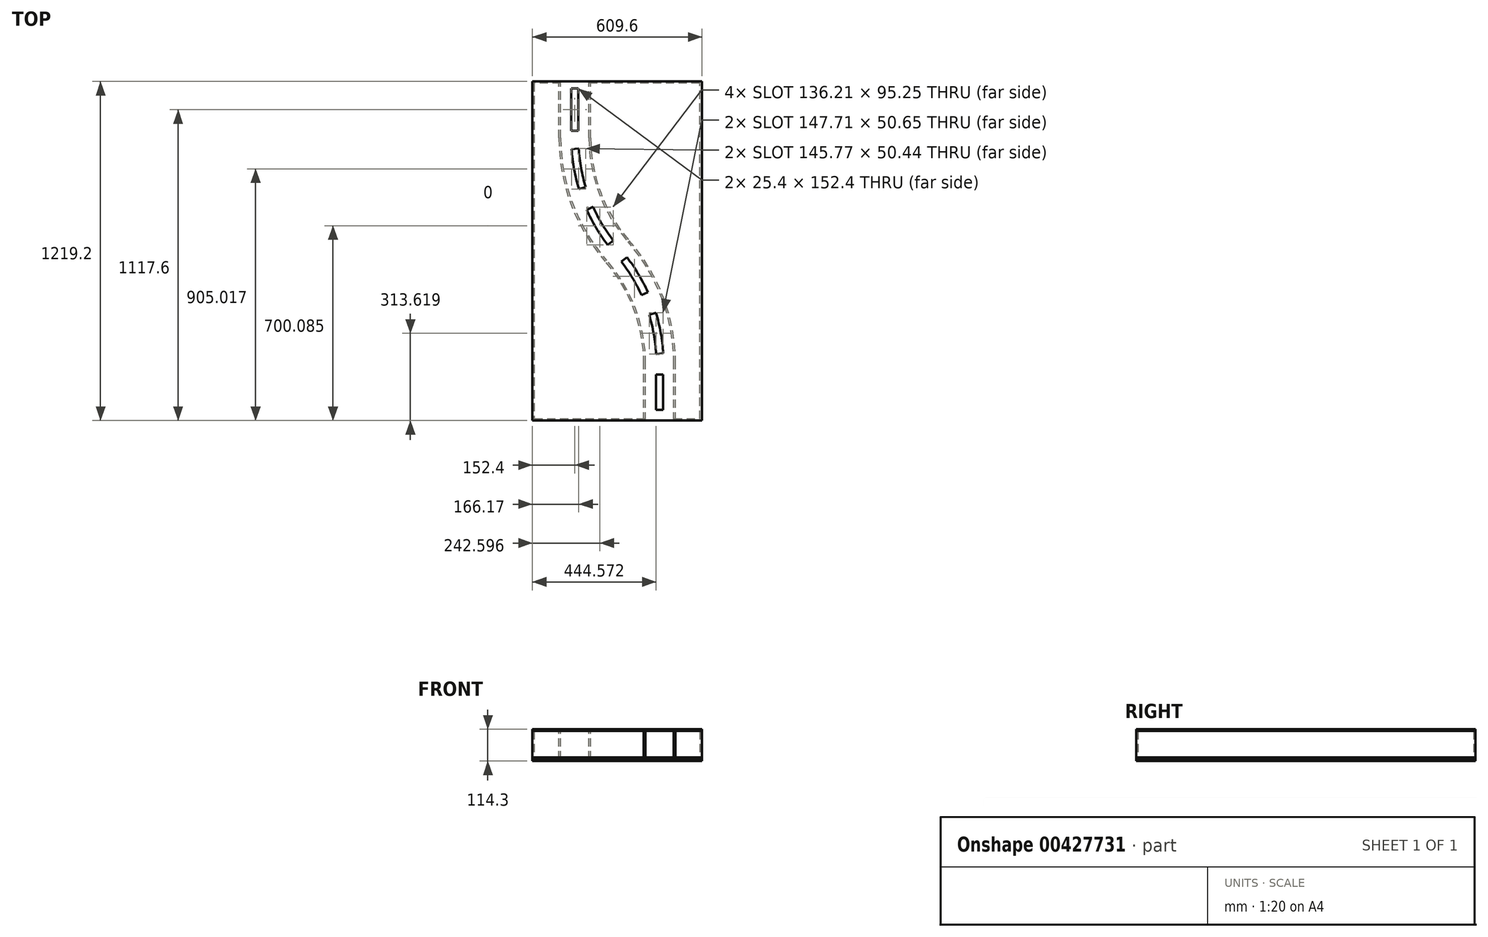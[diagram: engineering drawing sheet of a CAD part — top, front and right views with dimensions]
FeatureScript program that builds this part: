
annotation { "Feature Type Name" : "Feature", "Feature Type Description" : "" }
export const myFeature = defineFeature(function(context is Context, id is Id, definition is map)
    precondition{}
    {
        {
            var Q0;
            Q0=qCreatedBy(makeId("Top.planeOp"),FACE);
            var sketch = newSketch(context, id + "F0", { "sketchPlane" : qUnion([Q0])});
            skLineSegment(sketch, "E0.bottom", {"start": v(0, 0) * mm, "end": v(609.6, 0) * mm});
            skLineSegment(sketch, "E0.top", {"start": v(0, 1219.2) * mm, "end": v(609.6, 1219.2) * mm});
            skLineSegment(sketch, "E0.left", {"start": v(0, 0) * mm, "end": v(0, 1219.2) * mm});
            skLineSegment(sketch, "E0.right", {"start": v(609.6, 0) * mm, "end": v(609.6, 1219.2) * mm});
            skLineSegment(sketch, "E1", {"start": v(406.4, 0) * mm, "end": v(406.4, 203.2) * mm});
            skLineSegment(sketch, "E2", {"start": v(508, 0) * mm, "end": v(508, 203.2) * mm});
            skArc(sketch, "E3", {"start": v(406.4, 203.2) * mm, "mid": v(370.28, 402.38) * mm, "end": v(266.53, 576.2) * mm});
            skArc(sketch, "E4", {"start": v(508, 203.2) * mm, "mid": v(465.41, 438.05) * mm, "end": v(343.07, 643) * mm});
            skLineSegment(sketch, "E5", {"start": v(-160.87, 203.2) * mm, "end": v(343.07, 643) * mm, "construction": true});
            skArc(sketch, "E6", {"start": v(343.07, 643) * mm, "mid": v(239.32, 816.82) * mm, "end": v(203.2, 1016) * mm});
            skArc(sketch, "E7", {"start": v(266.53, 576.2) * mm, "mid": v(144.19, 781.15) * mm, "end": v(101.6, 1016) * mm});
            skLineSegment(sketch, "E8", {"start": v(770.47, 1016) * mm, "end": v(101.6, 1016) * mm, "construction": true});
            skLineSegment(sketch, "E9", {"start": v(101.6, 1016) * mm, "end": v(101.6, 1219.2) * mm});
            skLineSegment(sketch, "E10", {"start": v(203.2, 1016) * mm, "end": v(203.2, 1219.2) * mm});
            skLineSegment(sketch, "E11", {"start": v(239.32, 816.82) * mm, "end": v(144.19, 781.15) * mm, "construction": true});
            skLineSegment(sketch, "E12", {"start": v(370.28, 402.38) * mm, "end": v(465.41, 438.05) * mm, "construction": true});
            skLineSegment(sketch, "E13", {"start": v(406.4, 203.2) * mm, "end": v(508, 203.2) * mm, "construction": true});
            skLineSegment(sketch, "E14.bottom", {"start": v(139.7, 1041.4) * mm, "end": v(165.1, 1041.4) * mm});
            skLineSegment(sketch, "E14.top", {"start": v(139.7, 1193.8) * mm, "end": v(165.1, 1193.8) * mm});
            skLineSegment(sketch, "E14.left", {"start": v(139.7, 1041.4) * mm, "end": v(139.7, 1193.8) * mm});
            skLineSegment(sketch, "E14.right", {"start": v(165.1, 1041.4) * mm, "end": v(165.1, 1193.8) * mm});
            skLineSegment(sketch, "E15.bottom", {"start": v(444.5, 165.1) * mm, "end": v(469.9, 165.1) * mm});
            skLineSegment(sketch, "E15.top", {"start": v(444.5, 38.63) * mm, "end": v(469.9, 38.63) * mm});
            skLineSegment(sketch, "E15.left", {"start": v(444.5, 165.1) * mm, "end": v(444.5, 38.63) * mm});
            skLineSegment(sketch, "E15.right", {"start": v(469.9, 165.1) * mm, "end": v(469.9, 38.63) * mm});
            skArc(sketch, "E16", {"start": v(444.5, 239.77) * mm, "mid": v(436, 310.65) * mm, "end": v(419.25, 380.05) * mm});
            skArc(sketch, "E17", {"start": v(469.9, 241.3) * mm, "mid": v(461.05, 315.16) * mm, "end": v(443.59, 387.47) * mm});
            skLineSegment(sketch, "E18", {"start": v(443.59, 387.47) * mm, "end": v(-160.87, 203.2) * mm, "construction": true});
            skLineSegment(sketch, "E19", {"start": v(-160.87, 203.2) * mm, "end": v(469.9, 241.3) * mm, "construction": true});
            skLineSegment(sketch, "E20", {"start": v(444.5, 239.77) * mm, "end": v(469.9, 241.3) * mm});
            skLineSegment(sketch, "E21", {"start": v(419.25, 380.05) * mm, "end": v(443.59, 387.47) * mm});
            skArc(sketch, "E22", {"start": v(339.53, 587.22) * mm, "mid": v(380.74, 526.5) * mm, "end": v(414.63, 461.4) * mm});
            skArc(sketch, "E23", {"start": v(319.38, 571.75) * mm, "mid": v(358.93, 513.48) * mm, "end": v(391.45, 451.01) * mm});
            skLineSegment(sketch, "E24", {"start": v(-160.87, 203.2) * mm, "end": v(339.53, 587.22) * mm, "construction": true});
            skLineSegment(sketch, "E25", {"start": v(-160.87, 203.2) * mm, "end": v(414.63, 461.4) * mm, "construction": true});
            skLineSegment(sketch, "E26", {"start": v(319.38, 571.75) * mm, "end": v(339.53, 587.22) * mm});
            skLineSegment(sketch, "E27", {"start": v(391.45, 451.01) * mm, "end": v(414.63, 461.4) * mm});
            skLineSegment(sketch, "E28", {"start": v(770.47, 1016) * mm, "end": v(102.93, 973.9) * mm, "construction": true});
            skLineSegment(sketch, "E29", {"start": v(770.47, 1016) * mm, "end": v(130.65, 821.03) * mm, "construction": true});
            skArc(sketch, "E30", {"start": v(191.4, 839.54) * mm, "mid": v(174.81, 907.99) * mm, "end": v(166.3, 977.9) * mm});
            skArc(sketch, "E31", {"start": v(167.1, 832.13) * mm, "mid": v(149.82, 903.46) * mm, "end": v(140.95, 976.3) * mm});
            skLineSegment(sketch, "E32", {"start": v(140.95, 976.3) * mm, "end": v(166.3, 977.9) * mm});
            skLineSegment(sketch, "E33", {"start": v(167.1, 832.13) * mm, "end": v(191.4, 839.54) * mm});
            skLineSegment(sketch, "E34", {"start": v(770.47, 1016) * mm, "end": v(160.2, 742.2) * mm, "construction": true});
            skLineSegment(sketch, "E35", {"start": v(770.47, 1016) * mm, "end": v(239.85, 608.79) * mm, "construction": true});
            skArc(sketch, "E36", {"start": v(290.22, 647.45) * mm, "mid": v(250.67, 705.72) * mm, "end": v(218.15, 768.19) * mm});
            skArc(sketch, "E37", {"start": v(270.07, 631.98) * mm, "mid": v(228.86, 692.7) * mm, "end": v(194.97, 757.8) * mm});
            skLineSegment(sketch, "E38", {"start": v(194.97, 757.8) * mm, "end": v(218.15, 768.19) * mm});
            skLineSegment(sketch, "E39", {"start": v(270.07, 631.98) * mm, "end": v(290.22, 647.45) * mm});
            skSolve(sketch);
        }
        {
            var Q0;
            {var subQ0=sQuery(id+"F0.wireOp",EDGE,"E0.left");Q0=makeQuery(id+"F0.imprint","IMPRINT",FACE,{"disambiguationData":[TD([[makeQuery(id+"F0.imprint","IMPRINT",EDGE,{"derivedFrom":subQ0}),-1.0]])]});}
            var Q1;
            {var subQ0=sQuery(id+"F0.wireOp",EDGE,"E1");Q1=makeQuery(id+"F0.imprint","IMPRINT",FACE,{"disambiguationData":[TD([[makeQuery(id+"F0.imprint","IMPRINT",EDGE,{"derivedFrom":subQ0}),-1.0]])]});}
            var Q2;
            {var subQ1=sQuery(id+"F0.wireOp",EDGE,"E0.right");Q2=makeQuery(id+"F0.imprint","IMPRINT",FACE,{"disambiguationData":[TD([[makeQuery(id+"F0.imprint","IMPRINT",EDGE,{"derivedFrom":subQ1}),1.0]])]});}
            extrude(context, id + "F1", {"entities" : qUnion([Q0, Q1, Q2]), "oppositeDirection" : true, "depth" : 6.35 * mm});
        }
        {
            var Q0;
            Q0=makeQuery(id+"F1.opExtrude","SWEPT_FACE",FACE,{"disambiguationData":[OSD([sQuery(id+"F0.wireOp",EDGE,"E0.bottom")])]});
            var sketch = newSketch(context, id + "F2", { "sketchPlane" : qUnion([Q0])});
            skLineSegment(sketch, "E40.bottom", {"start": v(406.4, 0) * mm, "end": v(400.05, 0) * mm});
            skLineSegment(sketch, "E40.top", {"start": v(406.4, 101.6) * mm, "end": v(400.05, 101.6) * mm});
            skLineSegment(sketch, "E40.left", {"start": v(406.4, 0) * mm, "end": v(406.4, 101.6) * mm});
            skLineSegment(sketch, "E40.right", {"start": v(400.05, 0) * mm, "end": v(400.05, 101.6) * mm});
            skLineSegment(sketch, "E41.bottom", {"start": v(508, 0) * mm, "end": v(514.35, 0) * mm});
            skLineSegment(sketch, "E41.top", {"start": v(508, 101.6) * mm, "end": v(514.35, 101.6) * mm});
            skLineSegment(sketch, "E41.left", {"start": v(508, 0) * mm, "end": v(508, 101.6) * mm});
            skLineSegment(sketch, "E41.right", {"start": v(514.35, 0) * mm, "end": v(514.35, 101.6) * mm});
            skLineSegment(sketch, "E42", {"start": v(406.4, 101.6) * mm, "end": v(508, 101.6) * mm});
            skLineSegment(sketch, "E43", {"start": v(406.4, 101.6) * mm, "end": v(508, 0) * mm, "construction": true});
            skLineSegment(sketch, "E44", {"start": v(508, 101.6) * mm, "end": v(406.4, 0) * mm, "construction": true});
            skCircle(sketch, "E45", {"center": v(457.2, 50.8) * mm, "radius": 44.45 * mm});
            skSolve(sketch);
        }
        {
            var Q0;
            Q0=makeQuery(id+"F2.imprint","IMPRINT",FACE,{"disambiguationData":[TD([[makeQuery(id+"F2.imprint","IMPRINT",EDGE,{"derivedFrom":sQuery(id+"F2.wireOp",EDGE,"E40.bottom")}),1.0]])]});
            var Q1;
            Q1=sQuery(id+"F0.wireOp",EDGE,"E1");
            var Q2;
            Q2=sQuery(id+"F0.wireOp",EDGE,"E3");
            var Q3;
            Q3=sQuery(id+"F0.wireOp",EDGE,"E7");
            var Q4;
            Q4=sQuery(id+"F0.wireOp",EDGE,"E9");
            sweep(context, id + "F3", {"profiles" : qUnion([Q0]), "path" : qUnion([Q1, Q2, Q3, Q4])});
        }
        {
            var Q0;
            Q0=makeQuery(id+"F2.imprint","IMPRINT",FACE,{"disambiguationData":[TD([[makeQuery(id+"F2.imprint","IMPRINT",EDGE,{"derivedFrom":sQuery(id+"F2.wireOp",EDGE,"E41.bottom")}),1.0]])]});
            var Q1;
            Q1=sQuery(id+"F0.wireOp",EDGE,"E2");
            var Q2;
            Q2=sQuery(id+"F0.wireOp",EDGE,"E4");
            var Q3;
            Q3=sQuery(id+"F0.wireOp",EDGE,"E6");
            var Q4;
            Q4=sQuery(id+"F0.wireOp",EDGE,"E10");
            sweep(context, id + "F4", {"profiles" : qUnion([Q0]), "path" : qUnion([Q1, Q2, Q3, Q4])});
        }
        {
            var Q0;
            {var subQ1=sQuery(id+"F2.wireOp",EDGE,"E40.left");Q0=makeQuery(id+"F2.imprint","IMPRINT",FACE,{"disambiguationData":[TD([[makeQuery(id+"F2.imprint","IMPRINT",EDGE,{"derivedFrom":subQ1}),-1.0]])]});}
            extrude(context, id + "F5", {"entities" : qUnion([Q0]), "depth" : 6.35 * mm});
        }
        {
            var Q0;
            {var subQ0=sQuery(id+"F0.wireOp",EDGE,"E0.left");Q0=makeQuery(id+"F0.imprint","IMPRINT",FACE,{"disambiguationData":[TD([[makeQuery(id+"F0.imprint","IMPRINT",EDGE,{"derivedFrom":subQ0}),-1.0]])]});}
            var Q1;
            {var subQ1=sQuery(id+"F0.wireOp",EDGE,"E0.right");Q1=makeQuery(id+"F0.imprint","IMPRINT",FACE,{"disambiguationData":[TD([[makeQuery(id+"F0.imprint","IMPRINT",EDGE,{"derivedFrom":subQ1}),1.0]])]});}
            extrude(context, id + "F6", {"entities" : qUnion([Q0, Q1]), "depth" : 6.35 * mm});
        }
        {
            var Q0;
            {var subQ0=sQuery(id+"F0.wireOp",EDGE,"E1");Q0=makeQuery(id+"F0.imprint","IMPRINT",FACE,{"disambiguationData":[TD([[makeQuery(id+"F0.imprint","IMPRINT",EDGE,{"derivedFrom":subQ0}),-1.0]])]});}
            extrude(context, id + "F7", {"entities" : qUnion([Q0]), "operationType" : NewBodyOperationType.REMOVE, "oppositeDirection" : true, "depth" : 0.25 * mm});
        }
        {
            var Q0;
            {var subQ0=sQuery(id+"F0.wireOp",EDGE,"E0.left");var subQ1=sQuery(id+"F0.wireOp",EDGE,"E0.top");var subQ2=sQuery(id+"F0.wireOp",EDGE,"E0.bottom");Q0=makeQuery(id+"F7.boolean.opBoolean","SPLIT",FACE,{"disambiguationData":[TD([makeQuery(id+"F1.opExtrude","SWEPT_FACE",FACE,{"disambiguationData":[OSD([subQ0])]})])],"derivedFrom":makeQuery(id+"F1.opExtrude","CAP_FACE",FACE,{"disambiguationData":[OSD([subQ2,subQ1,subQ0,sQuery(id+"F0.wireOp",EDGE,"E0.right"),sQuery(id+"F0.wireOp",EDGE,"E14.bottom"),sQuery(id+"F0.wireOp",EDGE,"E14.top"),sQuery(id+"F0.wireOp",EDGE,"E14.left"),sQuery(id+"F0.wireOp",EDGE,"E14.right"),sQuery(id+"F0.wireOp",EDGE,"E15.bottom"),sQuery(id+"F0.wireOp",EDGE,"E15.top"),sQuery(id+"F0.wireOp",EDGE,"E15.left"),sQuery(id+"F0.wireOp",EDGE,"E15.right"),sQuery(id+"F0.wireOp",EDGE,"E16"),sQuery(id+"F0.wireOp",EDGE,"E17"),sQuery(id+"F0.wireOp",EDGE,"E20"),sQuery(id+"F0.wireOp",EDGE,"E21"),sQuery(id+"F0.wireOp",EDGE,"E22"),sQuery(id+"F0.wireOp",EDGE,"E23"),sQuery(id+"F0.wireOp",EDGE,"E26"),sQuery(id+"F0.wireOp",EDGE,"E27"),sQuery(id+"F0.wireOp",EDGE,"E30"),sQuery(id+"F0.wireOp",EDGE,"E31"),sQuery(id+"F0.wireOp",EDGE,"E32"),sQuery(id+"F0.wireOp",EDGE,"E33"),sQuery(id+"F0.wireOp",EDGE,"E36"),sQuery(id+"F0.wireOp",EDGE,"E37"),sQuery(id+"F0.wireOp",EDGE,"E38"),sQuery(id+"F0.wireOp",EDGE,"E39")])],"isStart":true})});}
            var sketch = newSketch(context, id + "F8", { "sketchPlane" : qUnion([Q0])});
            skLineSegment(sketch, "E46.0", {"start": v(0, 1219.2) * mm, "end": v(101.6, 1219.2) * mm});
            skLineSegment(sketch, "E47.0", {"start": v(0, 0) * mm, "end": v(0, 1219.2) * mm});
            skLineSegment(sketch, "E48.0", {"start": v(0, 0) * mm, "end": v(406.4, 0) * mm});
            skLineSegment(sketch, "E49.0", {"start": v(508, 0) * mm, "end": v(609.6, 0) * mm});
            skLineSegment(sketch, "E50.0", {"start": v(609.6, 0) * mm, "end": v(609.6, 1219.2) * mm});
            skLineSegment(sketch, "E51.0", {"start": v(203.2, 1219.2) * mm, "end": v(609.6, 1219.2) * mm});
            skLineSegment(sketch, "E52", {"start": v(101.6, 1219.2) * mm, "end": v(101.6, 1213.15) * mm});
            skLineSegment(sketch, "E53", {"start": v(101.6, 1213.15) * mm, "end": v(6.48, 1213.15) * mm});
            skLineSegment(sketch, "E54", {"start": v(6.48, 1213.15) * mm, "end": v(6.48, 6.58) * mm});
            skLineSegment(sketch, "E55", {"start": v(6.48, 6.58) * mm, "end": v(406.4, 6.58) * mm});
            skLineSegment(sketch, "E56", {"start": v(406.4, 6.58) * mm, "end": v(406.4, 0) * mm});
            skLineSegment(sketch, "E57", {"start": v(508, 0) * mm, "end": v(508, 6.58) * mm});
            skLineSegment(sketch, "E58", {"start": v(508, 6.58) * mm, "end": v(601.1, 6.58) * mm});
            skLineSegment(sketch, "E59", {"start": v(601.1, 6.58) * mm, "end": v(601.1, 1213.15) * mm});
            skLineSegment(sketch, "E60", {"start": v(601.1, 1213.15) * mm, "end": v(203.2, 1213.15) * mm});
            skLineSegment(sketch, "E61", {"start": v(203.2, 1213.15) * mm, "end": v(203.2, 1219.2) * mm});
            skSolve(sketch);
        }
        {
            var Q0;
            Q0=makeQuery(id+"F8.imprint","IMPRINT",FACE,{"disambiguationData":[TD([[makeQuery(id+"F8.imprint","IMPRINT",EDGE,{"derivedFrom":sQuery(id+"F8.wireOp",EDGE,"E46.0")}),-1.0]])]});
            var Q1;
            Q1=makeQuery(id+"F8.imprint","IMPRINT",FACE,{"disambiguationData":[TD([[makeQuery(id+"F8.imprint","IMPRINT",EDGE,{"derivedFrom":sQuery(id+"F8.wireOp",EDGE,"E49.0")}),1.0]])]});
            extrude(context, id + "F9", {"entities" : qUnion([Q0, Q1]), "depth" : 101.6 * mm});
        }
        {
            var Q0;
            Q0=makeQuery(id+"F5.opExtrude","SWEPT_BODY",BODY,{"disambiguationData":[OSD([sQuery(id+"F0.wireOp",EDGE,"E0.bottom"),sQuery(id+"F2.wireOp",EDGE,"E40.left"),sQuery(id+"F2.wireOp",EDGE,"E41.left"),sQuery(id+"F2.wireOp",EDGE,"E42"),sQuery(id+"F2.wireOp",EDGE,"E45")])]});
            deleteBodies(context, id + "F10", {"entities" : qUnion([Q0])});
        }
        {
            var Q0;
            {var subQ0=sQuery(id+"F0.wireOp",EDGE,"E0.left");Q0=makeQuery(id+"F0.imprint","IMPRINT",FACE,{"disambiguationData":[TD([[makeQuery(id+"F0.imprint","IMPRINT",EDGE,{"derivedFrom":subQ0}),-1.0]])]});}
            var Q1;
            {var subQ0=sQuery(id+"F0.wireOp",EDGE,"E1");Q1=makeQuery(id+"F0.imprint","IMPRINT",FACE,{"disambiguationData":[TD([[makeQuery(id+"F0.imprint","IMPRINT",EDGE,{"derivedFrom":subQ0}),-1.0]])]});}
            var Q2;
            {var subQ1=sQuery(id+"F0.wireOp",EDGE,"E0.right");Q2=makeQuery(id+"F0.imprint","IMPRINT",FACE,{"disambiguationData":[TD([[makeQuery(id+"F0.imprint","IMPRINT",EDGE,{"derivedFrom":subQ1}),1.0]])]});}
            extrude(context, id + "F11", {"entities" : qUnion([Q0, Q1, Q2]), "depth" : 107.95 * mm, "hasSecondDirection" : true, "secondDirectionOppositeDirection" : false, "secondDirectionDepth" : 101.6 * mm});
        }
    });
